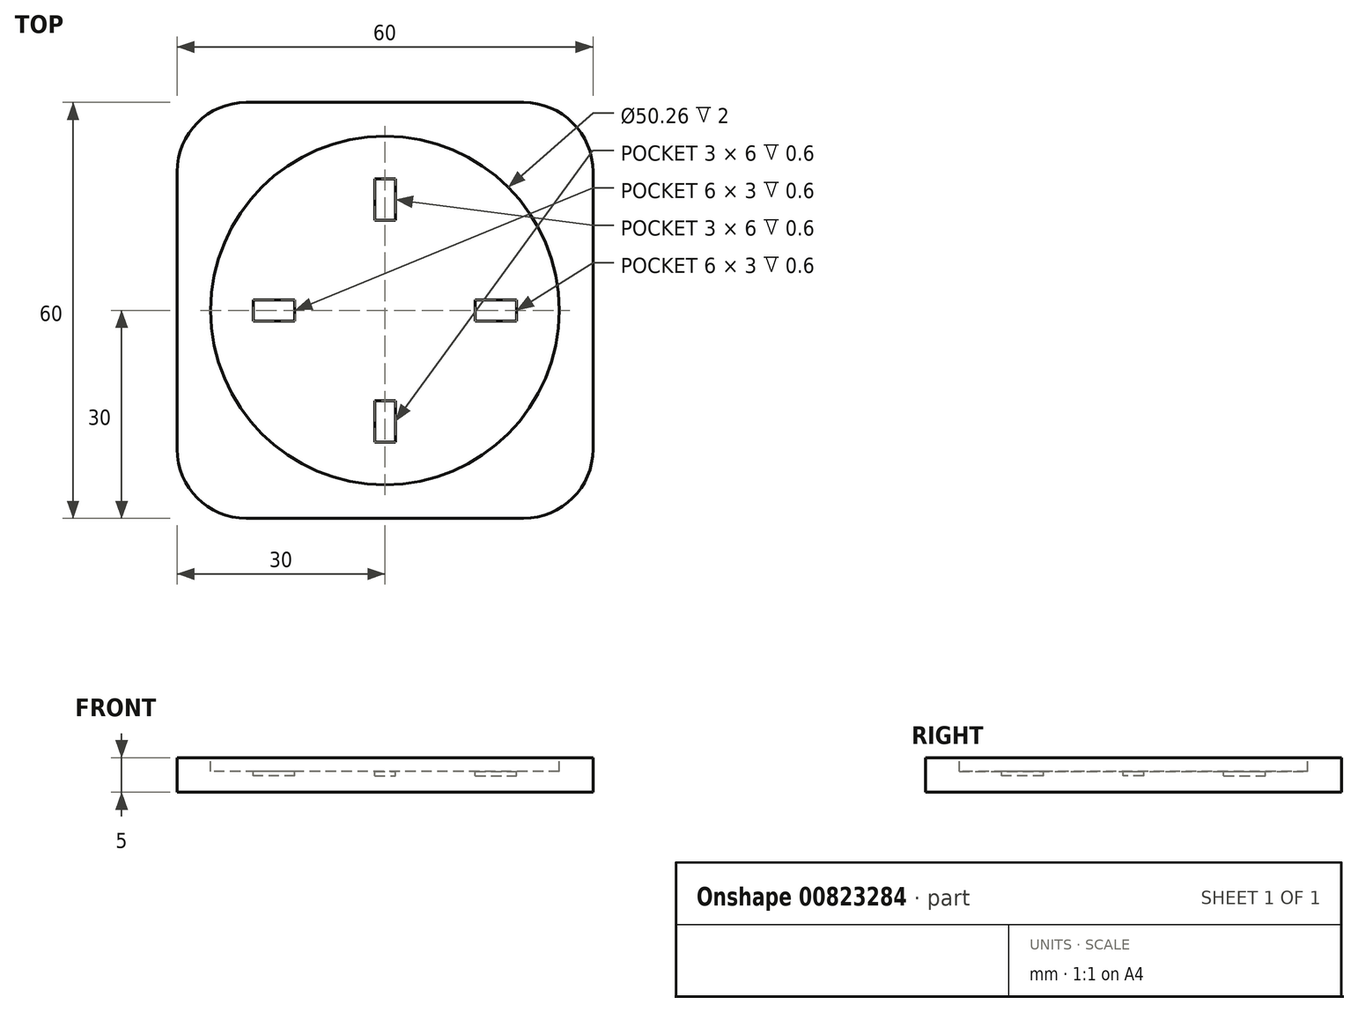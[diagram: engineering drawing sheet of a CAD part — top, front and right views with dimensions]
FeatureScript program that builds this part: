
annotation { "Feature Type Name" : "Feature", "Feature Type Description" : "" }
export const myFeature = defineFeature(function(context is Context, id is Id, definition is map)
    precondition{}
    {
        {
            var Q0;
            Q0=qCreatedBy(makeId("Top.planeOp"),FACE);
            var sketch = newSketch(context, id + "F0", { "sketchPlane" : qUnion([Q0])});
            skLineSegment(sketch, "E0.bottom", {"start": v(-30, 30) * mm, "end": v(30, 30) * mm});
            skLineSegment(sketch, "E0.top", {"start": v(-30, -30) * mm, "end": v(30, -30) * mm});
            skLineSegment(sketch, "E0.left", {"start": v(-30, 30) * mm, "end": v(-30, -30) * mm});
            skLineSegment(sketch, "E0.right", {"start": v(30, 30) * mm, "end": v(30, -30) * mm});
            skPoint(sketch, "E0.middle", {"position": v(0, 0) * mm});
            skSolve(sketch);
        }
        {
            var Q0;
            Q0=makeQuery(id+"F0.imprint","IMPRINT",FACE,{"disambiguationData":[TD([[makeQuery(id+"F0.imprint","IMPRINT",EDGE,{"derivedFrom":sQuery(id+"F0.wireOp",EDGE,"E0.bottom")}),-1.0]])]});
            extrude(context, id + "F1", {"entities" : qUnion([Q0]), "depth" : 5 * mm, "offsetDistance" : 25 * mm});
        }
        {
            var Q0;
            Q0=makeQuery(id+"F1.opExtrude","CAP_FACE",FACE,{"disambiguationData":[OSD([sQuery(id+"F0.wireOp",EDGE,"E0.bottom"),sQuery(id+"F0.wireOp",EDGE,"E0.top"),sQuery(id+"F0.wireOp",EDGE,"E0.left"),sQuery(id+"F0.wireOp",EDGE,"E0.right")])],"isStart":false});
            var sketch = newSketch(context, id + "F2", { "sketchPlane" : qUnion([Q0])});
            skCircle(sketch, "E1", {"center": v(0, 0) * mm, "radius": 25.13 * mm});
            skSolve(sketch);
        }
        {
            var Q0;
            Q0=makeQuery(id+"F2.imprint","IMPRINT",FACE,{"disambiguationData":[TD([[makeQuery(id+"F2.imprint","IMPRINT",EDGE,{"derivedFrom":sQuery(id+"F2.wireOp",EDGE,"E1")}),1.0]])]});
            extrude(context, id + "F3", {"entities" : qUnion([Q0]), "operationType" : NewBodyOperationType.REMOVE, "oppositeDirection" : true, "depth" : 2 * mm, "offsetDistance" : 25 * mm});
        }
        {
            var Q0;
            Q0=makeQuery(id+"F1.opExtrude","SWEPT_EDGE",EDGE,{"disambiguationData":[OSD([sQuery(id+"F0.wireOp",EDGE,"E0.bottom"),sQuery(id+"F0.wireOp",EDGE,"E0.right")])]});
            var Q1;
            Q1=makeQuery(id+"F1.opExtrude","SWEPT_EDGE",EDGE,{"disambiguationData":[OSD([sQuery(id+"F0.wireOp",EDGE,"E0.top"),sQuery(id+"F0.wireOp",EDGE,"E0.right")])]});
            var Q2;
            Q2=makeQuery(id+"F1.opExtrude","SWEPT_EDGE",EDGE,{"disambiguationData":[OSD([sQuery(id+"F0.wireOp",EDGE,"E0.top"),sQuery(id+"F0.wireOp",EDGE,"E0.left")])]});
            var Q3;
            Q3=makeQuery(id+"F1.opExtrude","SWEPT_EDGE",EDGE,{"disambiguationData":[OSD([sQuery(id+"F0.wireOp",EDGE,"E0.bottom"),sQuery(id+"F0.wireOp",EDGE,"E0.left")])]});
            fillet(context, id + "F4", {"entities" : qUnion([Q0, Q1, Q2, Q3]), "radius" : 10 * mm, "tangentPropagation" : true, "allowEdgeOverflow" : false});
        }
        {
            var Q0;
            Q0=makeQuery(id+"F3.boolean.opBoolean","COPY",FACE,{"derivedFrom":makeQuery(id+"F3.opExtrude","CAP_FACE",FACE,{"disambiguationData":[OSD([sQuery(id+"F2.wireOp",EDGE,"E1")])],"isStart":false})});
            var sketch = newSketch(context, id + "F5", { "sketchPlane" : qUnion([Q0])});
            skLineSegment(sketch, "E2.bottom", {"start": v(1.5, 13) * mm, "end": v(-1.5, 13) * mm});
            skLineSegment(sketch, "E2.top", {"start": v(1.5, 19) * mm, "end": v(-1.5, 19) * mm});
            skLineSegment(sketch, "E2.left", {"start": v(1.5, 13) * mm, "end": v(1.5, 19) * mm});
            skLineSegment(sketch, "E2.right", {"start": v(-1.5, 13) * mm, "end": v(-1.5, 19) * mm});
            skPoint(sketch, "E2.middle", {"position": v(0, 16) * mm});
            skLineSegment(sketch, "E3.1.0", {"start": v(-19, 1.5) * mm, "end": v(-19, -1.5) * mm});
            skLineSegment(sketch, "E3.1.1", {"start": v(-13, -1.5) * mm, "end": v(-19, -1.5) * mm});
            skLineSegment(sketch, "E3.1.2", {"start": v(-13, 1.5) * mm, "end": v(-19, 1.5) * mm});
            skLineSegment(sketch, "E3.1.3", {"start": v(-13, 1.5) * mm, "end": v(-13, -1.5) * mm});
            skLineSegment(sketch, "E3.2.0", {"start": v(-1.5, -19) * mm, "end": v(1.5, -19) * mm});
            skLineSegment(sketch, "E3.2.1", {"start": v(1.5, -13) * mm, "end": v(1.5, -19) * mm});
            skLineSegment(sketch, "E3.2.2", {"start": v(-1.5, -13) * mm, "end": v(-1.5, -19) * mm});
            skLineSegment(sketch, "E3.2.3", {"start": v(-1.5, -13) * mm, "end": v(1.5, -13) * mm});
            skLineSegment(sketch, "E3.3.0", {"start": v(19, -1.5) * mm, "end": v(19, 1.5) * mm});
            skLineSegment(sketch, "E3.3.1", {"start": v(13, 1.5) * mm, "end": v(19, 1.5) * mm});
            skLineSegment(sketch, "E3.3.2", {"start": v(13, -1.5) * mm, "end": v(19, -1.5) * mm});
            skLineSegment(sketch, "E3.3.3", {"start": v(13, -1.5) * mm, "end": v(13, 1.5) * mm});
            skPoint(sketch, "E3.center", {"position": v(0, 0) * mm});
            skSolve(sketch);
        }
        {
            var Q0;
            Q0=makeQuery(id+"F5.imprint","IMPRINT",FACE,{"disambiguationData":[TD([[makeQuery(id+"F5.imprint","IMPRINT",EDGE,{"derivedFrom":sQuery(id+"F5.wireOp",EDGE,"E3.3.0")}),1.0]])]});
            var Q1;
            Q1=makeQuery(id+"F5.imprint","IMPRINT",FACE,{"disambiguationData":[TD([[makeQuery(id+"F5.imprint","IMPRINT",EDGE,{"derivedFrom":sQuery(id+"F5.wireOp",EDGE,"E2.bottom")}),-1.0]])]});
            var Q2;
            Q2=makeQuery(id+"F5.imprint","IMPRINT",FACE,{"disambiguationData":[TD([[makeQuery(id+"F5.imprint","IMPRINT",EDGE,{"derivedFrom":sQuery(id+"F5.wireOp",EDGE,"E3.1.0")}),1.0]])]});
            var Q3;
            Q3=makeQuery(id+"F5.imprint","IMPRINT",FACE,{"disambiguationData":[TD([[makeQuery(id+"F5.imprint","IMPRINT",EDGE,{"derivedFrom":sQuery(id+"F5.wireOp",EDGE,"E3.2.0")}),1.0]])]});
            extrude(context, id + "F6", {"entities" : qUnion([Q0, Q1, Q2, Q3]), "operationType" : NewBodyOperationType.REMOVE, "oppositeDirection" : true, "depth" : 0.6 * mm, "offsetDistance" : 25 * mm});
        }
    });
